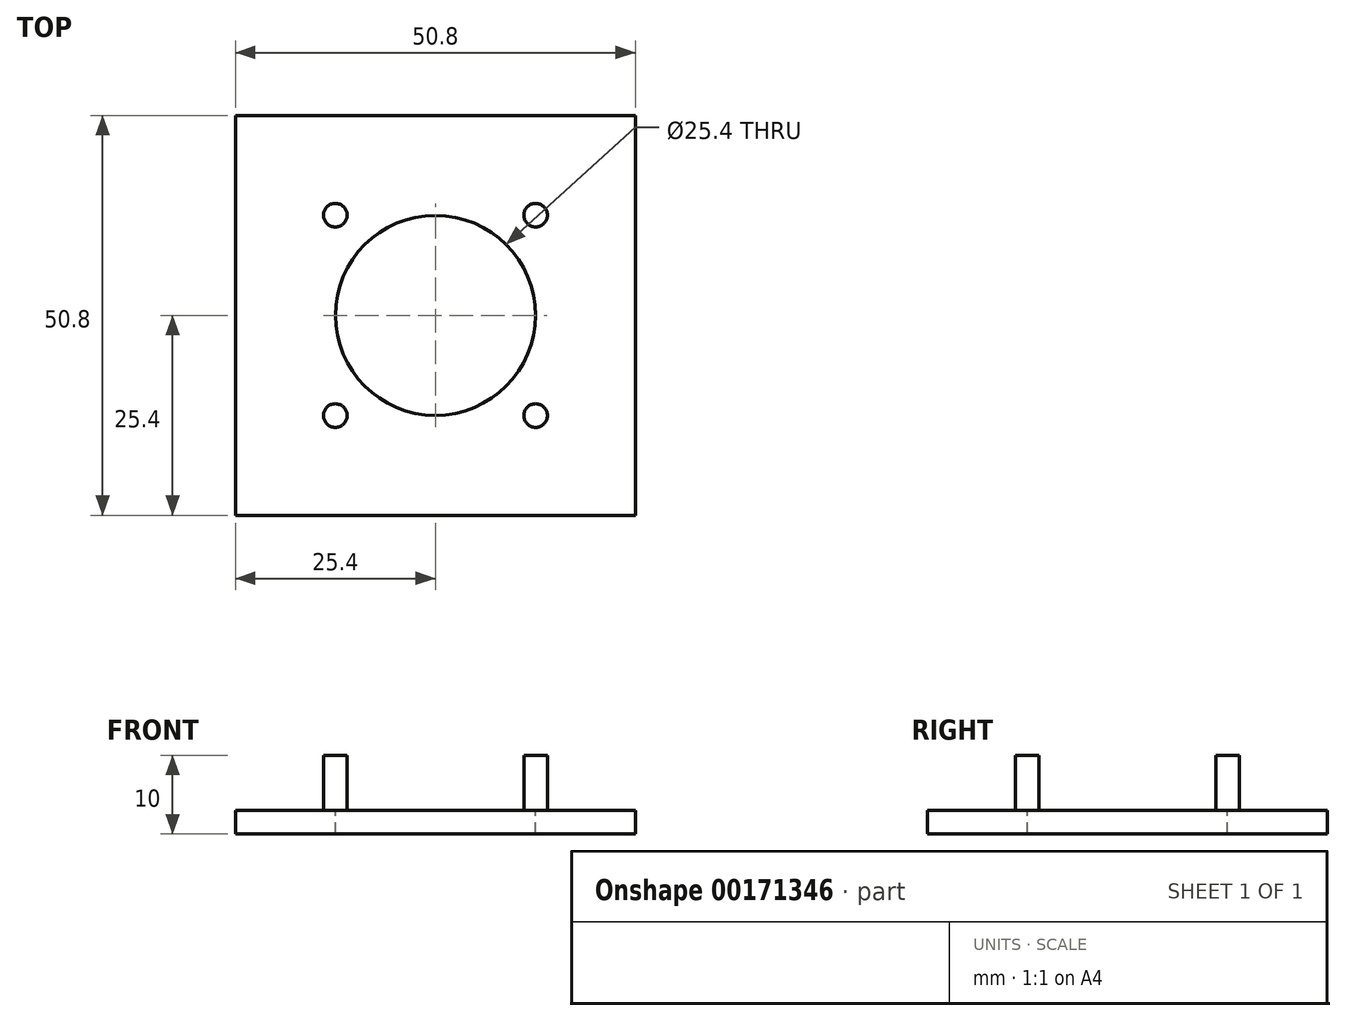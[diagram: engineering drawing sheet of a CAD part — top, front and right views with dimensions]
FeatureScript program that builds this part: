
annotation { "Feature Type Name" : "Feature", "Feature Type Description" : "" }
export const myFeature = defineFeature(function(context is Context, id is Id, definition is map)
    precondition{}
    {
        {
            var Q0;
            Q0=qCreatedBy(makeId("Top.planeOp"),FACE);
            var sketch = newSketch(context, id + "F0", { "sketchPlane" : qUnion([Q0])});
            skCircle(sketch, "E0", {"center": v(0, 0) * mm, "radius": 25.4 * mm, "construction": true});
            skLineSegment(sketch, "E1.bottom", {"start": v(-25.4, 25.4) * mm, "end": v(25.4, 25.4) * mm});
            skLineSegment(sketch, "E1.top", {"start": v(-25.4, -25.4) * mm, "end": v(25.4, -25.4) * mm});
            skLineSegment(sketch, "E1.left", {"start": v(-25.4, 25.4) * mm, "end": v(-25.4, -25.4) * mm});
            skLineSegment(sketch, "E1.right", {"start": v(25.4, 25.4) * mm, "end": v(25.4, -25.4) * mm});
            skLineSegment(sketch, "E2", {"start": v(-25.4, 25.4) * mm, "end": v(25.4, -25.4) * mm, "construction": true});
            skSolve(sketch);
        }
        {
            var Q0;
            Q0 = qSketchRegion(id + "F0", true);
            extrude(context, id + "F1", {"entities" : qUnion([Q0]), "depth" : 3 * mm});
        }
        {
            var Q0;
            Q0=qCreatedBy(makeId("Top.planeOp"),FACE);
            var sketch = newSketch(context, id + "F2", { "sketchPlane" : qUnion([Q0])});
            skCircle(sketch, "E3", {"center": v(0, 0) * mm, "radius": 18 * mm, "construction": true});
            skLineSegment(sketch, "E4", {"start": v(0, 0) * mm, "end": v(-25.4, 25.4) * mm, "construction": true});
            skCircle(sketch, "E5", {"center": v(-12.73, 12.73) * mm, "radius": 1.5 * mm});
            skCircle(sketch, "E6.1.0", {"center": v(-12.73, -12.73) * mm, "radius": 1.5 * mm});
            skCircle(sketch, "E6.2.0", {"center": v(12.73, -12.73) * mm, "radius": 1.5 * mm});
            skCircle(sketch, "E6.3.0", {"center": v(12.73, 12.73) * mm, "radius": 1.5 * mm});
            skSolve(sketch);
        }
        {
            var Q0;
            Q0 = qSketchRegion(id + "F2", true);
            extrude(context, id + "F3", {"entities" : qUnion([Q0]), "operationType" : NewBodyOperationType.ADD, "depth" : 10 * mm});
        }
        {
            var Q0;
            Q0=makeQuery(id+"F1.opExtrude","CAP_FACE",FACE,{"disambiguationData":[OSD([sQuery(id+"F0.wireOp",EDGE,"E1.bottom"),sQuery(id+"F0.wireOp",EDGE,"E1.top"),sQuery(id+"F0.wireOp",EDGE,"E1.left"),sQuery(id+"F0.wireOp",EDGE,"E1.right")])],"isStart":false});
            var sketch = newSketch(context, id + "F4", { "sketchPlane" : qUnion([Q0])});
            skCircle(sketch, "E7", {"center": v(0, 0) * mm, "radius": 12.7 * mm});
            skSolve(sketch);
        }
        {
            var Q0;
            Q0 = qSketchRegion(id + "F4", true);
            extrude(context, id + "F5", {"entities" : qUnion([Q0]), "operationType" : NewBodyOperationType.REMOVE, "oppositeDirection" : true, "depth" : 25.4 * mm});
        }
    });
